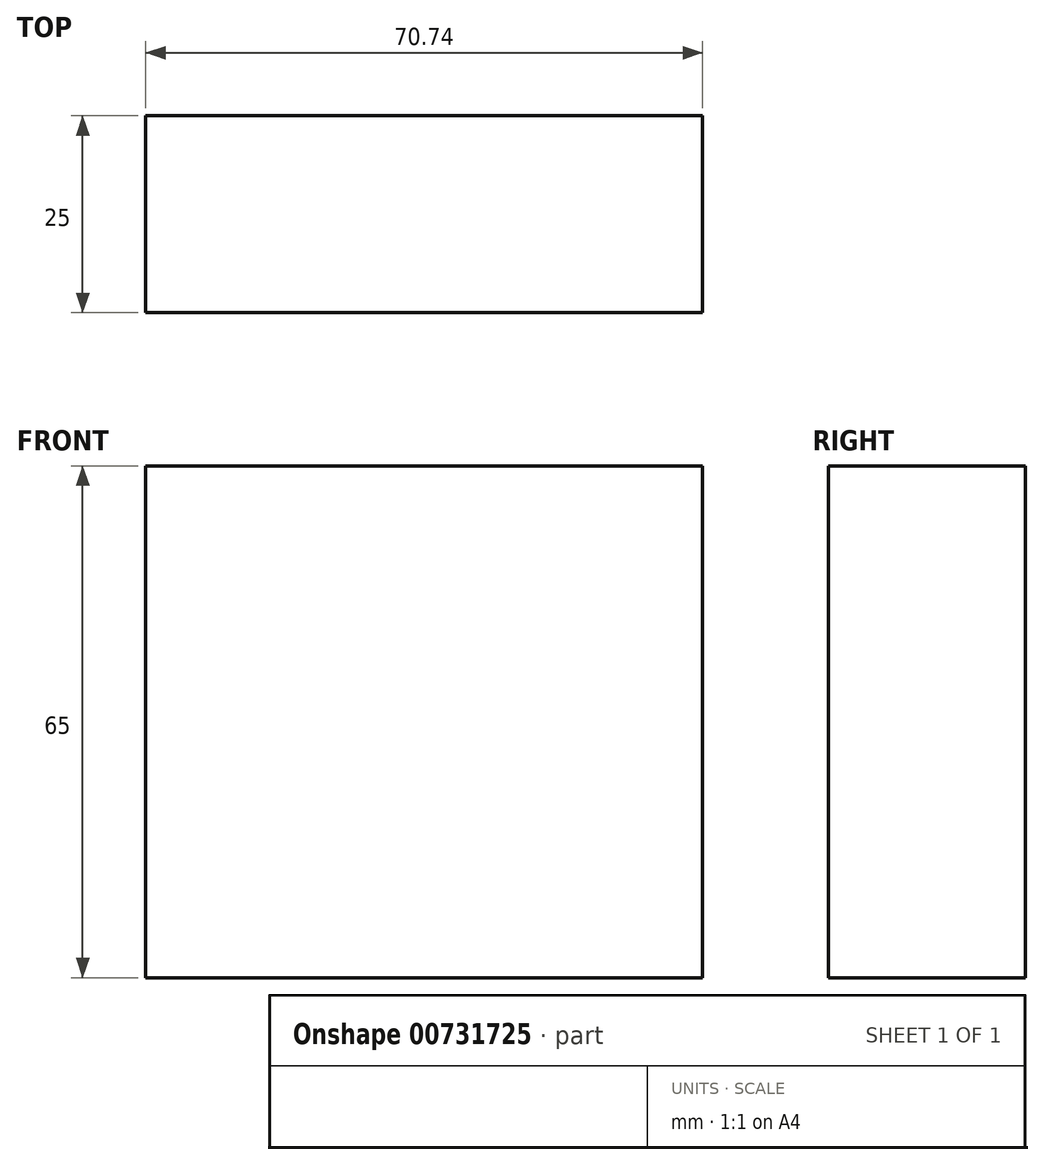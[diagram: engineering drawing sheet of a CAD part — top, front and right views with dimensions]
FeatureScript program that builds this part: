
annotation { "Feature Type Name" : "Feature", "Feature Type Description" : "" }
export const myFeature = defineFeature(function(context is Context, id is Id, definition is map)
    precondition{}
    {
        {
            var Q0;
            Q0=qCreatedBy(makeId("Front.planeOp"),FACE);
            var sketch = newSketch(context, id + "F0", { "sketchPlane" : qUnion([Q0])});
            skLineSegment(sketch, "E0.bottom", {"start": v(-33.67, 30) * mm, "end": v(37.07, 30) * mm});
            skLineSegment(sketch, "E0.top", {"start": v(-33.67, -35) * mm, "end": v(37.07, -35) * mm});
            skLineSegment(sketch, "E0.left", {"start": v(-33.67, 30) * mm, "end": v(-33.67, -35) * mm});
            skLineSegment(sketch, "E0.right", {"start": v(37.07, 30) * mm, "end": v(37.07, -35) * mm});
            skSolve(sketch);
        }
        {
            var Q0;
            Q0=makeQuery(id+"F0.imprint","IMPRINT",FACE,{"disambiguationData":[TD([[makeQuery(id+"F0.imprint","IMPRINT",EDGE,{"derivedFrom":sQuery(id+"F0.wireOp",EDGE,"E0.bottom")}),-1.0]])]});
            extrude(context, id + "F1", {"entities" : qUnion([Q0]), "depth" : 25 * mm, "offsetDistance" : 25 * mm});
        }
    });
